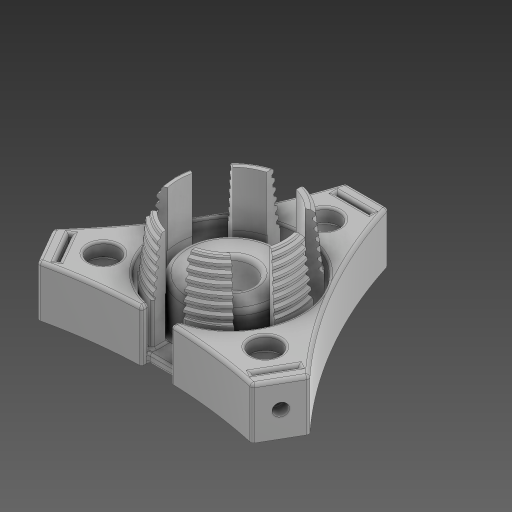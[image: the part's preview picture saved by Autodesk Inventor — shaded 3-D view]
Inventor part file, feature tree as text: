
AUTODESK INVENTOR PART (.ipt)
format: ipt  version: 2024 (Build 280153000, 153)  size: 1,865,216 bytes
history: native  units: mm
features: sketch x17, extrude x12, fillet x9, chamfer x3, hole x3, pattern_circular x3, helix x2, plane x2, projected_geometry x2, draft x1
ambient origin geometry x8: Origin, YZ Plane, XZ Plane, XY Plane, X Axis, Y Axis, Z Axis, Center Point
bodies: Solid1 (feature_tree)
feature tree (54):
  extrude  "Extrusion1"  Depth=29.5mm
  draft  "FaceDraft1"
  sketch  "Sketch2"  dims[d7=6.806784mm d8=0.55605mm]
  helix  "Coil1"  [1 undecoded]
  helix  "Coil2"  [1 undecoded]
  extrude  "Extrusion2"  Depth=0.55605mm
  extrude  "Extrusion3"  TaperAngle=0.0deg  [1 undecoded]
  fillet  "Fillet1"  [1 undecoded]
  chamfer  "Chamfer1"  Distance=0.3mm Angle=45.0deg
  plane  "Work Plane1"
  extrude  "Extrusion4"  TaperAngle=0.0deg  [1 undecoded]
  extrude  "Extrusion8"  Depth=60.0mm TaperAngle=360.0deg
  hole  "Hole2"  [1 undecoded]
  sketch  "Sketch13"  dims[d58=6.0mm d65=60.0mm d67=360.0deg]
  extrude  "Extrusion11"  Depth=10.0mm TaperAngle=0.0deg
  sketch  "Sketch18"  dims[d91=33.0mm d92=12.0mm d93=0.0mm]
  fillet  "Fillet9"  Radius=31.2mm
  extrude  "Extrusion15"  Depth=31.967mm
  hole  "Hole5"  [1 undecoded]
  pattern_circular  "Circular Pattern5"  Count=3 Angle=360.0deg
  plane  "Work Plane4"
  extrude  "Extrusion16"  TaperAngle=0.0deg  [1 undecoded]
  fillet  "Fillet14"  Radius=0.75mm
  extrude  "Extrusion17"  Depth=22.0mm
  extrude  "Extrusion19"  Depth=10.0mm TaperAngle=0.0deg
  fillet  "Fillet17"  Radius=32.8mm
  fillet  "Fillet18"  Radius=9.0mm
  extrude  "Extrusion20"  Depth=0.5mm
  fillet  "Fillet20"  Radius=0.25mm
  chamfer  "Chamfer6"  Distance=7.0mm
  pattern_circular  "Circular Pattern6"  Count=6 Angle=360.0deg
  hole  "Bearing Hole"  [1 undecoded]
  chamfer  "Chamfer7"  Distance=3.2mm
  pattern_circular  "Circular Pattern7"  [2 undecoded]
  extrude  "Extrusion21"  Depth=0.5mm
  fillet  "Fillet21"  [1 undecoded]
  fillet  "Fillet22"  Radius=0.75mm
  fillet  "Fillet23"  Radius=0.75mm
  sketch  "Sketch1"  dims[d0=24.7mm d1=29.5mm d2=12.875mm d3=0.0mm d4=1.047198mm]
  projected_geometry  "Projected Loop1"
  sketch  "Sketch3"  dims[d9=6.806784mm]
  sketch  "Sketch4"  dims[d10=2.0mm d11=10.0mm d12=70.0mm d13=-1.047198mm d14=90.0deg d15=90.0deg d16=0.0mm d17=0.0mm d18=0.6mm]
  sketch  "Sketch5"  dims[d19=2.0mm d20=10.0mm d21=10.0mm d22=1.047198mm d23=90.0deg d24=90.0deg d25=0.0mm d26=0.0mm d27=0.0mm d28=0.0mm d29=0.0mm d30=0.0mm]
  sketch  "Sketch10"  dims[d31=0.6mm d32=0.3mm d33=2.0mm d34=45.0deg]
  sketch  "Sketch11"  dims[d36=-2.0mm d42=0.0mm d43=0.0mm]
  sketch  "Sketch21"  dims[d94=5.3mm d95=6.0mm d96=10.0mm d97=7.0mm d98=90.0deg d99=8.0mm d100=20.594885mm d122=10.0mm d123=0.0mm d124=31.2mm]
  sketch  "Sketch22"  dims[d150=1.0mm d166=31.967mm]
  sketch  "Sketch25"  dims[d167=10.0mm d168=30.0deg]
  sketch  "Sketch26"  dims[d169=7.0mm d170=0.0mm]
  sketch  "Sketch28"  dims[d171=3.0mm d172=6.0mm d173=9.779mm d174=7.62mm d175=90.0deg d176=4.0mm d177=0.0mm d179=30.0mm d180=360.0deg]
  sketch  "Sketch29"  dims[d182=16.0mm d183=0.0mm d184=0.0mm d185=0.75mm]
  sketch  "Sketch30"  dims[d188=25.0mm d189=22.0mm]
  sketch  "Sketch31"  dims[d190=31.0mm d191=10.0mm d192=0.0mm d193=32.8mm d208=9.0mm d209=0.0mm d210=1.0mm d211=0.25mm d213=7.0mm d214=60.0mm d216=360.0deg d218=8.0mm d219=3.2mm d220=0.6mm d221=0.3mm d222=0.0mm d223=0.0mm d224=0.75mm d225=0.75mm d226=2.0mm d227=45.0deg d228=30.0mm d229=360.0deg d231=6.0mm d232=6.804mm d233=6.0mm d234=9.829mm d235=8.89mm d236=90.0deg d237=8.0mm d238=20.594885mm d239=22.0mm d240=17.5mm d241=1.5mm d242=2.0mm d243=45.0deg d244=30.0mm d245=360.0deg d248=2.0mm d249=13.962634mm d250=7.0mm d251=0.0mm d252=0.5mm d253=0.65mm d254=0.5mm d151=0.872665mm d152=0.5mm d153=0.872665mm d164=0.0mm d165=0.0mm]
  projected_geometry  "Project Cut Edges3"
note: 12 required parameter values undecoded (feature->parameter linkage not recoverable at this tier; creation-order binding heuristic only, values carry confidence <= 0.55)
